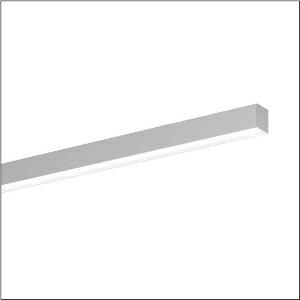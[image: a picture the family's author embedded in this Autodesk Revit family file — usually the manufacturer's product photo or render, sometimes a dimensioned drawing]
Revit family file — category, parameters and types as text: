
# Revit family: silica_r__21_51mx20tat2s_7558
name_source: partatom
category: Lighting Fixtures
units: mm (PartAtom-declared; Revit-internal decimal feet)

## family parameters
Cut with Voids When Loaded = No
Host = Face
Light Source = No
Part Type = Normal
Room Calculation Point = No
Round Connector Dimension = Use Diameter
Shared = No

## types (1)
- --- (1 x LED, 2400 lm, 20.5 W, 6500K)
    Apparent Load = 21 VA
    CIE Flux Codes = 48 79 96 100 100
    Color Rendering = 80
    Color Temperature = 6500K
    Default Elevation = 1800 mm
    Description = Silica® 21, office luminaire, primary optical cover: cover, of PMMA, opal, light emission: direct distribution, primary light characteristic: symmetric, installation type: surface-mounted, LED, rated luminous flux: 2.400lm, luminous efficacy: 112lm/W, light colour: 8tw, colour temperature: 2700..6500K, control gear: ECG DALI, with terminal, 3+2-pole, max. 2.5mm², mains connection: 220..240V, AC, 50/60Hz, rated input power: 21.5W, luminaire housing, of aluminium, metallic grey (RAL 9006), length: 1.204mm, width: 53mm, height: 53mm, protection rating (complete): IP20, insulation class (complete): insulation class I (protective earthing), certification: CE, permissible operating ambient temperature: 0..+35°C, standard: EN 50419, packaging unit: 1 piece
    Height = 0 mm  [stored 0 ft]
    Lamp = 1 x LED
    Lamp Light Flux = 2400 lm
    Lamp Power = 20.5 W
    Lamp count = 1
    Length = 1204 mm
    Luminous efficacy = 117 lm/W
    Manufacturer = Siteco
    ModVariant = No
    Model = 51MX20TAT2S
    Mounting Place = Ceiling
    Mounting Type = Recessed
    Number of Poles = 1
    OnlyDefault = Yes
    Power Factor = 1
    Product Name = Silica® 21
    Product group = office luminaire | ceiling recessed
    ProductGroupID = 400
    Protection Class = Protection class I
    Protection Degree = IP 20
    RLX_Detail_Level = 1
    RLX_Emergency_Light_Flux = 0 lm
    RLX_Emergency_Type = 0
    RLX_Emergency_Type_DB = No
    RlxData = <blob elided: 23165 chars, md5=9a843f8e>
    Socket = socket
    Standby Power = 0 W
    System Light Flux = 2400 lm
    System Power = 21 W
    Type Comments = individual setting
    Type Image = l_1335933.jpg
    URL = http://relux.com
    VarID = @adj_109477
    Voltage = 0 V
    Weight = 0.00 kg
    Width = 53 mm

note: [stored X ft] marks values corroborated as IEEE doubles in the binary element streams (Revit-internal decimal feet)

## geometry (parser evidence)
native form markers: Blend x4, Sweep x12
no freeform markers — native parametric forms only
